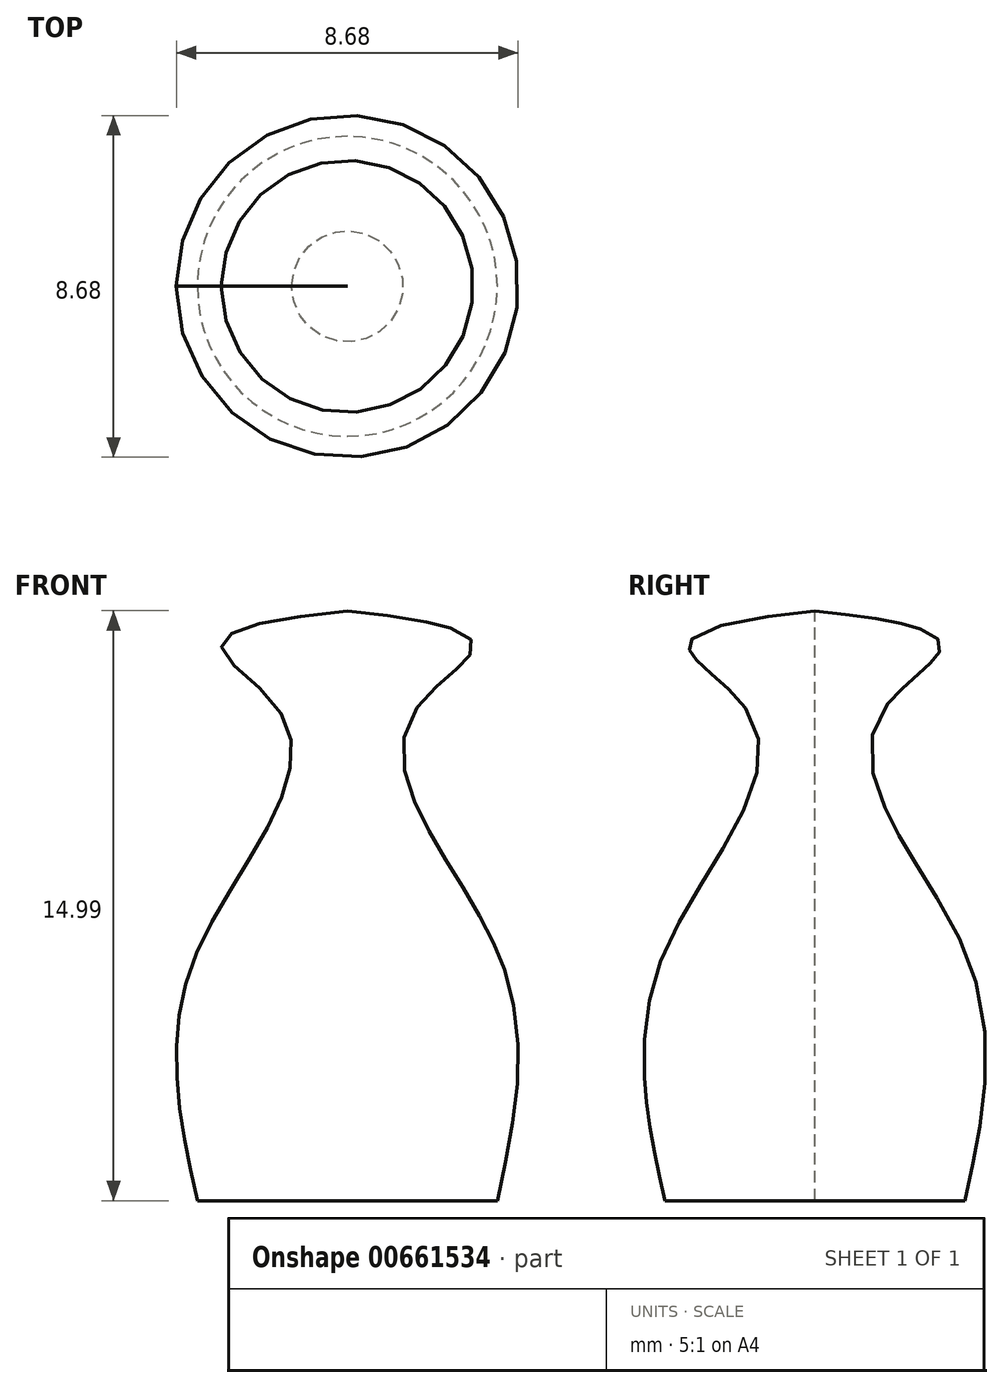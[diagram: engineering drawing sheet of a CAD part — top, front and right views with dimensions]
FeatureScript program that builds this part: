
annotation { "Feature Type Name" : "Feature", "Feature Type Description" : "" }
export const myFeature = defineFeature(function(context is Context, id is Id, definition is map)
    precondition{}
    {
        {
            var Q0;
            Q0=qCreatedBy(makeId("Top.planeOp"),FACE);
            var sketch = newSketch(context, id + "F0", { "sketchPlane" : qUnion([Q0])});
            skCircle(sketch, "E0", {"center": v(0, 0) * mm, "radius": 3.81 * mm});
            skSolve(sketch);
        }
        {
            var Q0;
            Q0=qCreatedBy(makeId("Top.planeOp"),FACE);
            cPlane(context, id + "F1", {"entities" : qUnion([Q0]), "cplaneType" : CPlaneType.OFFSET, "offset" : 6.35 * mm, "width" : 152.4 * mm, "height" : 152.4 * mm});
        }
        {
            var Q0;
            Q0=qCreatedBy(id+"F1.planeOp",FACE);
            var sketch = newSketch(context, id + "F2", { "sketchPlane" : qUnion([Q0])});
            skCircle(sketch, "E1", {"center": v(0, 0) * mm, "radius": 3.8 * mm});
            skSolve(sketch);
        }
        {
            var Q0;
            Q0=qCreatedBy(makeId("Top.planeOp"),FACE);
            cPlane(context, id + "F3", {"entities" : qUnion([Q0]), "cplaneType" : CPlaneType.OFFSET, "offset" : 12.7 * mm, "width" : 152.4 * mm, "height" : 152.4 * mm});
        }
        {
            var Q0;
            Q0=qCreatedBy(id+"F3.planeOp",FACE);
            var sketch = newSketch(context, id + "F4", { "sketchPlane" : qUnion([Q0])});
            skCircle(sketch, "E2", {"center": v(0, 0) * mm, "radius": 1.9 * mm});
            skSolve(sketch);
        }
        {
            var Q0;
            Q0=qCreatedBy(makeId("Top.planeOp"),FACE);
            cPlane(context, id + "F5", {"entities" : qUnion([Q0]), "cplaneType" : CPlaneType.OFFSET, "offset" : 13.97 * mm, "width" : 152.4 * mm, "height" : 152.4 * mm});
        }
        {
            var Q0;
            Q0=qCreatedBy(id+"F5.planeOp",FACE);
            var sketch = newSketch(context, id + "F6", { "sketchPlane" : qUnion([Q0])});
            skCircle(sketch, "E3", {"center": v(0, 0) * mm, "radius": 3.18 * mm});
            skSolve(sketch);
        }
        {
            var Q0;
            Q0=qCreatedBy(makeId("Top.planeOp"),FACE);
            cPlane(context, id + "F7", {"entities" : qUnion([Q0]), "cplaneType" : CPlaneType.OFFSET, "offset" : 15 * mm, "width" : 152.4 * mm, "height" : 152.4 * mm});
        }
        {
            var Q0;
            Q0=qCreatedBy(id+"F7.planeOp",FACE);
            var sketch = newSketch(context, id + "F8", { "sketchPlane" : qUnion([Q0])});
            skCircle(sketch, "E4", {"center": v(0, 0) * mm, "radius": 0.13 * mm});
            skSolve(sketch);
        }
        {
            var Q0;
            Q0=makeQuery(id+"F0.imprint","IMPRINT",FACE,{"disambiguationData":[TD([[makeQuery(id+"F0.imprint","IMPRINT",EDGE,{"derivedFrom":sQuery(id+"F0.wireOp",EDGE,"E0")}),1.0]])]});
            var Q1;
            Q1=makeQuery(id+"F2.imprint","IMPRINT",FACE,{"disambiguationData":[TD([[makeQuery(id+"F2.imprint","IMPRINT",EDGE,{"derivedFrom":sQuery(id+"F2.wireOp",EDGE,"E1")}),1.0]])]});
            var Q2;
            Q2=makeQuery(id+"F4.imprint","IMPRINT",FACE,{"disambiguationData":[TD([[makeQuery(id+"F4.imprint","IMPRINT",EDGE,{"derivedFrom":sQuery(id+"F4.wireOp",EDGE,"E2")}),1.0]])]});
            var Q3;
            Q3=makeQuery(id+"F6.imprint","IMPRINT",FACE,{"disambiguationData":[TD([[makeQuery(id+"F6.imprint","IMPRINT",EDGE,{"derivedFrom":sQuery(id+"F6.wireOp",EDGE,"E3")}),1.0]])]});
            var Q4;
            Q4=sQuery(id+"F8.wireOp",VERTEX,"E4.center");
            loft(context, id + "F9", {"sheetProfilesArray" : [{ "sheetProfileEntities" : qUnion([Q0]) }, { "sheetProfileEntities" : qUnion([Q1]) }, { "sheetProfileEntities" : qUnion([Q2]) }, { "sheetProfileEntities" : qUnion([Q3]) }, { "sheetProfileEntities" : qUnion([Q4]) }]});
        }
    });
